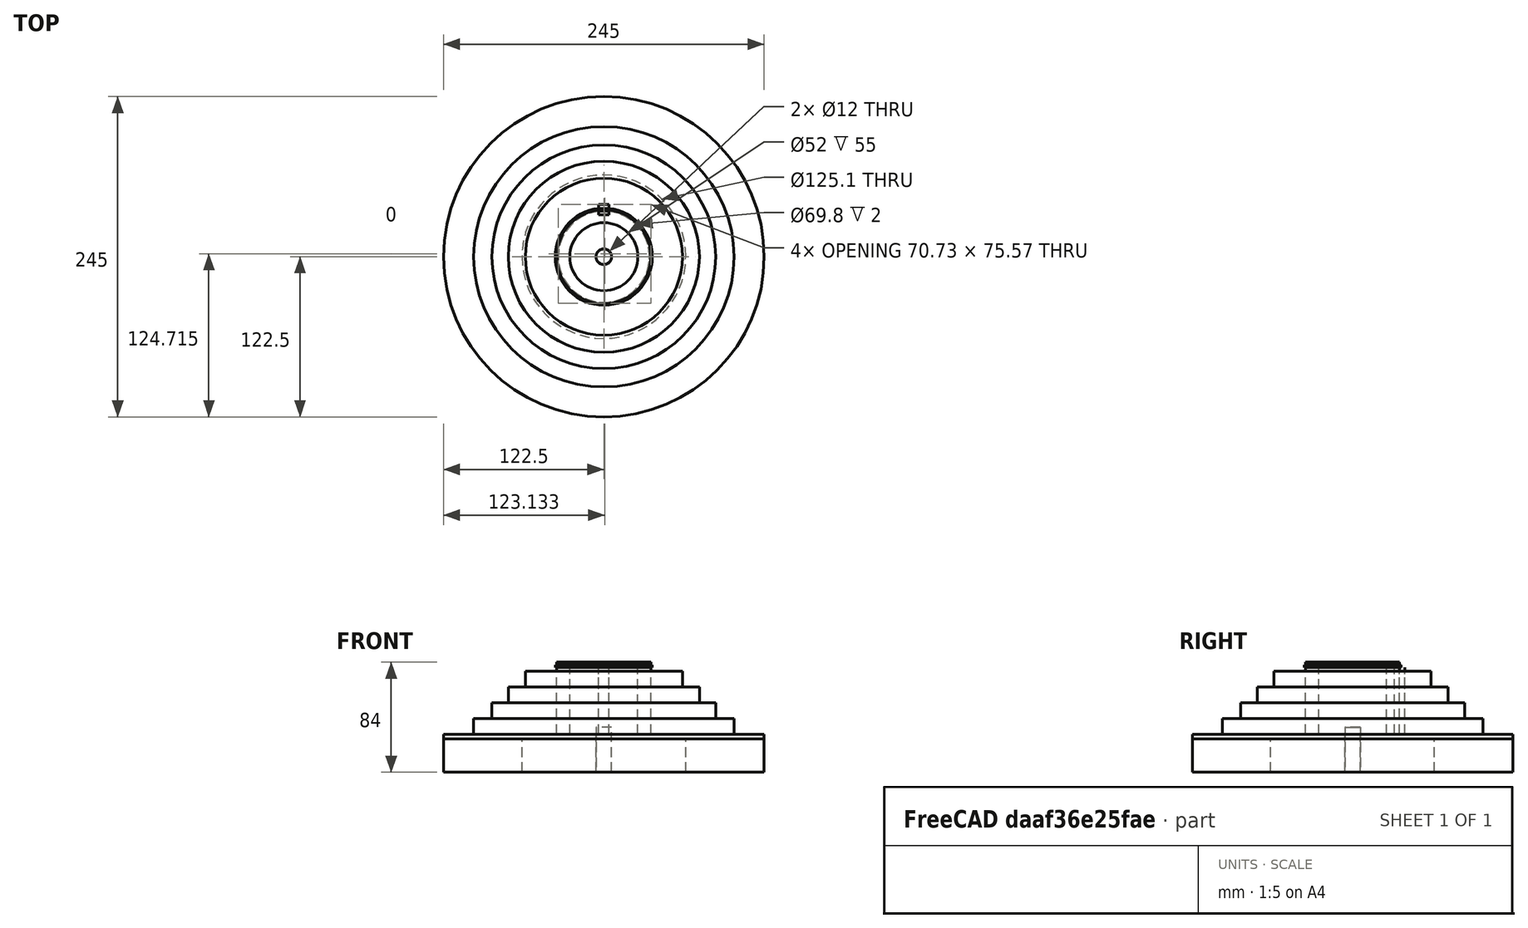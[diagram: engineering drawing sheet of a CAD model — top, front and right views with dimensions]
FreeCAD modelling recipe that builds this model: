
FCSTD DOCUMENT  (FreeCAD 1.0R39319 (Git))
Label: inertia_cylinder-custom
License: All rights reserved
LicenseURL: https://en.wikipedia.org/wiki/All_rights_reserved
objects: TechDraw::DrawViewDimension×42, Part::FeaturePython×10, TechDraw::DrawProjGroupItem×9, Part::Cut×5, TechDraw::DrawSVGTemplate×5, TechDraw::DrawViewAnnotation×5, TechDraw::DrawViewImage×5, TechDraw::DrawPage×5, Spreadsheet::Sheet×4, Part::Compound×3, Part::Box×2, App::DocumentObjectGroup×2, TechDraw::DrawViewSection×2, Part::Cylinder×1, PartDesign::FeatureBase×1, PartDesign::Body×1, Part::MultiFuse×1
note: 89 computed .brp shape members not serialized (recipe doc carries the construction recipe); baked Part::Feature solids carry a one-line shape summary decoded from their .brp

FEATURE [Spreadsheet::Sheet] Spreadsheet  label="fixedParameters"
  cells = A1='spacial properties; I1(color_scale)='color scale; A2='tubes; B2='radiusInner; C2='radiusOuter; D2='length; J2='Have to confirm; A3='contactDrum; B3(contactDrum_radiusInner)==threadedRod_radius; C3(contactDrum_radiusOuter)==25.14 mm; D3(contactDrum_length)==80.84 mm; J3='taken from spreadsheet; A4='disk; B4(disk_radiusInner)==threadedRod_radius; C4(disk_radiusOuter)==62.55 mm; D4(disk_length)==25.23 mm; J4='irrelevant but have to confirm; C5=125.11; J5='irrelevant; A6='cylinders; B6='radius; C6='length; A7='threadedRod; B7(threadedRod_radius)==6 mm; C7(threadedShaft_extrusionLength)==8.97 mm; A8='wheel; B8(wheel_radius)==0.3406 m; C8(wheel_length)==47 mm; A10='clearanceSpace; B10='horizontal; C10='vertical; D10='vertical mid; A11='diskFrame; B11(diskFrame_h_clearance)==68 mm; C11(diskFrame_v_clearance)==120 mm; D11==39 mm; A13='matter properties; A14='mass; B14='bike; A15='mass; B15(bike_mass)==15 kg; A17='materials; B17='density; A18='stainlessSteel; B18(ss_density)==7.85 g / ml; A19='dMetal; B19(dMetal_density)==ss_density; A20='all; B20='density; C20='mass; A21='wheel; B21='non-uniform-mix; C21(wheel_mass)==2 kg; A22='contactDrum; B22(contactDrum_density)==dMetal_density; A23='disk; B23(disk_density)==dMetal_density; A24='threadedRod; B24(threadedRod_density)==dMetal_density; A25='flywheel; B25(flywheel_density)==ss_density; A26='hub; B26(hub_density)==ss_density; A27='extendingDrum; B27(extendingDrum_density)==ss_density; A28='weightPlate; B28(weightPlate_density)==ss_density; A29='wp_ed_key; B29(wp_ed_key_density)==ss_density; A30='keyHandle; B30(keyHandle_density)==ss_density; A31='plateSecurer_screw; B31(plateSecurer_screw_density)==ss_density; A32='plateSecurerPlate; B32(plateSecurer_plateDensity)==ss_density; A33='constants; B33='Value; A34='pi; B34(pi_value)=3.1415
FEATURE [Spreadsheet::Sheet] Spreadsheet001  label="calculatedParameters"
  cells = A1='tubes; B1='radiusInner; C1='radiusOuter; D1='length; E1='density; F1='mass; G1='area out; H1='area in; I1='area; J1='Volume; A2='contactDrum; B2(contactDrum_radiusInner)==<<fixedParameters>>.contactDrum_radiusInner; C2(contactDrum_radiusOuter)==<<fixedParameters>>.contactDrum_radiusOuter; D2(contactDrum_length)==<<fixedParameters>>.contactDrum_length; E2(contactDrum_density)==<<fixedParameters>>.contactDrum_density; F2(contactDrum_mass)==<<fixedParameters>>.contactDrum_density * contactDrum_volume; G2(contactDrum_areaOut)==contactDrum_radiusOuter * contactDrum_radiusOuter * <<fixedParameters>>.pi_value; H2(contactDrum_areaIn)==contactDrum_radiusInner * contactDrum_radiusInner * <<fixedParameters>>.pi_value; I2(contactDrum_area)==contactDrum_areaOut - contactDrum_areaIn; J2(contactDrum_volume)==contactDrum_area * contactDrum_length; A3='disk; B3(disk_radiusInner)==<<fixedParameters>>.disk_radiusInner; C3(disk_radiusOuter)==<<fixedParameters>>.disk_radiusOuter; D3(disk_length)==<<fixedParameters>>.disk_length; E3(disk_density)==<<fixedParameters>>.disk_density; F3(disk_mass)==<<fixedParameters>>.disk_density * disk_volume; G3(disk_areaOut)==disk_radiusOuter * disk_radiusOuter * <<fixedParameters>>.pi_value; H3(disk_areaIn)==disk_radiusInner * disk_radiusInner * <<fixedParameters>>.pi_value; I3(disk_area)==disk_areaOut - disk_areaIn; J3(disk_volume)==disk_area * disk_length; A4='flywheel; B4(flywheel_radiusInner)==disk_radiusOuter; C4(flywheel_radiusOuter)==flywheel_radiusInner + <<properties>>.flywheel_radThickness; D4(flywheel_length)==<<fixedParameters>>.disk_length; E4(flywheel_density)==<<fixedParameters>>.flywheel_density; F4(flywheel_mass)==<<fixedParameters>>.flywheel_density * flywheel_volume; G4(flywheel_areaOut)==flywheel_radiusOuter * flywheel_radiusOuter * <<fixedParameters>>.pi_value; H4(flywheel_areaIn)==flywheel_radiusInner * flywheel_radiusInner * <<fixedParameters>>.pi_value; I4(flywheel_area)==flywheel_areaOut - flywheel_areaIn; J4(flywheel_volume)==flywheel_area * flywheel_length; A5='hub; B5(hub_radiusInner)==<<fixedParameters>>.threadedRod_radius; C5(hub_radiusOuter)==flywheel_radiusOuter; D5(hub_length)==<<properties>>.hub_thickness; E5(hub_density)==<<fixedParameters>>.hub_density; F5(hub_mass)==hub_volume * <<fixedParameters>>.hub_density; G5(hub_areaOut)==hub_radiusOuter * hub_radiusOuter * <<fixedParameters>>.pi_value; H5(hub_areaIn)==hub_radiusInner * hub_radiusInner * <<fixedParameters>>.pi_value; I5(hub_area)==hub_areaOut - hub_areaIn; J5(hub_volume)==hub_area * hub_length; A6='extendingDrum; B6(extendingDrum_radiusInner)==<<properties>>.nut_clearance; C6(extendingDrum_radiusOuter)==extendingDrum_radiusInner + <<properties>>.extendingDrum_radiusThickness; D6(extendingDrum_length)==<<fixedParameters>>.diskFrame_h_clearance - <<properties>>.weightPlate_thickness - <<properties>>.weightPlate_insertionTolerance; E6(extendingDrum_density)==<<fixedParameters>>.extendingDrum_density; F6(extendingDrum_mass)==<<fixedParameters>>.extendingDrum_density * extendingDrum_volume; G6(extendingDrum_areaOut)==extendingDrum_radiusOuter * extendingDrum_radiusOuter * <<fixedParameters>>.pi_value; H6(extendingDrum_areaIn)==extendingDrum_radiusInner * extendingDrum_radiusInner * <<fixedParameters>>.pi_value; I6(extendingDrum_area)==extendingDrum_areaOut - extendingDrum_areaIn; J6(extendingDrum_volume)==extendingDrum_area * extendingDrum_length; A7='w1; B7(weightPlate_radiusInner)==extendingDrum_radiusOuter; C7(w1_radiusOuter)==99.5 mm; D7(weightPlate_thickness)==<<properties>>.weightPlate_thickness; E7(weightPlate_density)==<<fixedParameters>>.weightPlate_density; F7(w1_mass)==w1_volume * weightPlate_density; G7(w1_areaOut)==w1_radiusOuter * w1_radiusOuter * <<fixedParameters>>.pi_value; H7(w_areaIn)==weightPlate_radiusInner * weightPlate_radiusInner * <<fixedParameters>>.pi_value; I7(w1_area)==w1_areaOut - w_areaIn; J7(w1_volume)==w1_area * weightPlate_thickness; A8='w2; C8(w2_radiusOuter)==85.5 mm; F8(w2_mass)==w2_volume * weightPlate_density; G8(w2_areaOut)==w2_radiusOuter * w2_radiusOuter * <<fixedParameters>>.pi_value; I8(w2_area)==w2_areaOut - w_areaIn; J8(w2_volume)==w2_area * weightPlate_thickness; A9='w3; C9(w3_radiusOuter)==73 mm; F9(w3_mass)==w3_volume * weightPlate_density; G9(w3_areaOut)==w3_radiusOuter * w3_radiusOuter * <<fixedParameters>>.pi_value; I9(w3_area)==w3_areaOut - w_areaIn; J9(w3_volume)==w3_area * weightPlate_thickness; A10='w4; C10(w4_radiusOuter)==60 mm; F10(w4_mass)==w4_volume * weightPlate_density; G10(w4_areaOut)==w4_radiusOuter * w4_radiusOuter * <<fixedParameters>>.pi_value; I10(w4_area)==w4_areaOut - w_areaIn; J10(w4_volume)==w4_area * weightPlate_thickness; A12='cuboids; B12='height; C12='width; D12='length; F12='mass; G12='area; A13='weightPlate_extendingDisk_key; B13(wp_ed_key_height)==<<properties>>.wP_eD_penetrationHeight; C13(wp_ed_key_width)==<<properties>>.wP_eD_key_penetrationWidth; D13(wp_ed_key_length)==extendingDrum_length; E13(wp_ed_key_density)==<<fixedParameters>>.wp_ed_key_density; F13(wp_ed_key_mass)==wp_ed_key_volume * wp_ed_key_density; G13(wp_ed_key_area)==wp_ed_key_height * wp_ed_key_width; J13(wp_ed_key_volume)==wp_ed_key_area * wp_ed_key_length; A14='cylinders; B14='radius; D14='length; E14='density; F14='mass; G14='area; J14='volume; A15='threadedShaft; B15(threadedShaft_radius)==<<fixedParameters>>.threadedRod_radius; D15(threadedShaft_length)==<<fixedParameters>>.threadedShaft_extrusionLength + disk_length; E15(threadedShaft_density)==<<fixedParameters>>.threadedRod_density; F15(threadedShaft_mass)==threadedShaft_volume * threadedShaft_density; G15(threadedShaft_area)==threadedShaft_radius * threadedShaft_radius * <<fixedParameters>>.pi_value; J15(threadedShaft_volume)==threadedShaft_area * threadedShaft_length; A16='wheel; B16(wheel_radius)==<<fixedParameters>>.wheel_radius; D16(wheel_length)==<<fixedParameters>>.wheel_length; E16(wheel_density)==wheel_mass / wheel_volume; F16(wheel_mass)==<<fixedParameters>>.wheel_mass; G16(wheel_area)==wheel_radius * wheel_radius * <<fixedParameters>>.pi_value; J16(wheel_volume)==wheel_length * wheel_area; A18='TOTAL for setup; F18==sum(F4:F10; F13); J18==sum(J4:J10; J13); A20='negative; A21='negative tubes; A22='circlip_grove; B22(circlip_grove_radiusInner)==circlip_grove_radiusOuter - <<properties>>.circlip_grove_depth; C22(circlip_grove_radiusOuter)==extendingDrum_radiusOuter; D22(circlip_grove_length)==<<properties>>.circlip_grove_width
FEATURE [Spreadsheet::Sheet] Spreadsheet002  label="properties"
  cells = A1='spacial properties; A2='tubes; B2='radius 'thickness; D2='key; E2='penetrationHeight; F2='penetrationWidth; A3='flywheel; B3(flywheel_radThickness)==59.95 mm; D3='weightPlate_extendingDrum_key; E3(wP_eD_penetrationHeight)==8 mm; F3(wP_eD_key_penetrationWidth)==8 mm; A4='extendingDrum; B4(extendingDrum_radiusThickness)==10 mm; D4='key; E4='extraLength; A5='tubes; B5='extending thickness; D5='key; E5(key_extraLength)==0 mm; A6='hub; B6(hub_thickness)==3.77 mm; A7='weightPlate; B7(weightPlate_thickness)==1.2 cm; D7='plateSecurer; E7='screwLength; F7='plateSecuringRadius; G7='plateThickness; D8='plateSecurer; E8(plateSecurer_screwLength)==1 cm; F8(plateSecuring_plate_radius)==5 cm; G8(plateSecurer_plateHeight)==2 mm; A9='tolerance; B9='insertionTolerance; A10='weightPlate; B10(weightPlate_insertionTolerance)==1 mm; D10='grove circlip; E10='width; F10='depth; G10='gap; A11='tolerance; B11='fittingTolerance; D11='circlip; E11(circlip_grove_width)==2 mm; F11(circlip_grove_depth)==1.1 mm; G11(circlip_grove_gap)==2 mm; A12='fitting tolerance; B12(fittingTolerance)==0.08 mm; D13='nut; E13='clearance for nut; A14='matter properties; D14='tool; E14(nut_clearance)==25.79 mm + 0.21 mm; A15='target mass; B15='mass; A16='rider; B16(rider_mass)==70 kg
FEATURE [Part::FeaturePython] Tube  label="flywheel"  # WARN: FeaturePython — macro-defined, semantics opaque (R4)
  AttacherType = Attacher::AttachEngine3D
  Height = 25.23
  InnerRadius = 62.55
  OuterRadius = 122.5
  expr: Height = <<calculatedParameters>>.flywheel_length
  expr: InnerRadius = <<calculatedParameters>>.flywheel_radiusInner
  expr: OuterRadius = <<calculatedParameters>>.flywheel_radiusOuter
FEATURE [Part::FeaturePython] Tube001  label="disk"  # WARN: FeaturePython — macro-defined, semantics opaque (R4)
  AttacherType = Attacher::AttachEngine3D
  Height = 25.23
  InnerRadius = 6
  OuterRadius = 62.55
  expr: Height = <<fixedParameters>>.disk_length
  expr: InnerRadius = <<fixedParameters>>.disk_radiusInner
  expr: OuterRadius = <<fixedParameters>>.disk_radiusOuter
FEATURE [Part::FeaturePython] Tube002  label="hub"  # WARN: FeaturePython — macro-defined, semantics opaque (R4)
  AttacherType = Attacher::AttachEngine3D
  Height = 3.77
  InnerRadius = 6
  OuterRadius = 122.5
  Placement = pos=(0,0,25.23) rot=(0,0,1;0rad)
  expr: .Placement.Base.z = <<flywheel>>.Placement.Base.z + <<calculatedParameters>>.flywheel_length
  expr: Height = <<calculatedParameters>>.hub_length
  expr: InnerRadius = <<calculatedParameters>>.hub_radiusInner
  expr: OuterRadius = <<calculatedParameters>>.hub_radiusOuter
FEATURE [Part::FeaturePython] Tube003  label="extendingDrum"  # WARN: FeaturePython — macro-defined, semantics opaque (R4)
  AttacherType = Attacher::AttachEngine3D
  Height = 55
  InnerRadius = 26
  OuterRadius = 36
  Placement = pos=(0,0,29) rot=(0,0,1;0rad)
  expr: .Placement.Base.z = <<hub>>.Placement.Base.z + <<calculatedParameters>>.hub_length
  expr: Height = <<calculatedParameters>>.extendingDrum_length
  expr: InnerRadius = <<calculatedParameters>>.extendingDrum_radiusInner
  expr: OuterRadius = <<calculatedParameters>>.extendingDrum_radiusOuter
FEATURE [Part::Box] Box  label="wp_ed_key"
  AttacherType = Attacher::AttachEngine3D
  Height = 55
  Length = 8
  Placement = pos=(-4,32,29) rot=(0,0,1;0rad)
  Width = 8
  expr: .Placement.Base.x = -<<calculatedParameters>>.wp_ed_key_width / 2
  expr: .Placement.Base.y = <<extendingDrum>>.OuterRadius - <<calculatedParameters>>.wp_ed_key_height / 2
  expr: .Placement.Base.z = <<hub>>.Placement.Base.z + <<calculatedParameters>>.hub_length
  expr: Height = <<calculatedParameters>>.wp_ed_key_length
  expr: Length = <<calculatedParameters>>.wp_ed_key_width
  expr: Width = <<calculatedParameters>>.wp_ed_key_height
FEATURE [Spreadsheet::Sheet] Spreadsheet003  label="inertia"
  cells = A1='addonSetup; C1='moment of inertia; D1='inertia; E1='ideal moi; F1='error; H1='moi per effective kg; I1='plate weights required; A2='tubes; B2='contactDrum; C2(moi_contactDrum)==<<calculatedParameters>>.contactDrum_radiusOuter * <<calculatedParameters>>.contactDrum_radiusOuter * <<calculatedParameters>>.contactDrum_mass * 0.5 - <<calculatedParameters>>.contactDrum_radiusInner * <<calculatedParameters>>.contactDrum_radiusInner * <<calculatedParameters>>.contactDrum_mass * 0.5; D2==0 kg; H2(moi_pkg)==625 (mm ^ 2); I2(w1_t_kg)==20 kg; B3='disk; C3(moi_disk)==<<calculatedParameters>>.disk_radiusOuter * <<calculatedParameters>>.disk_radiusOuter * <<calculatedParameters>>.disk_mass * 0.5 - <<calculatedParameters>>.disk_radiusInner * <<calculatedParameters>>.disk_radiusInner * <<calculatedParameters>>.disk_mass * 0.5; I3(w2_t_kg)==10 kg; B4='flywheel; C4(moi_flywheel)==<<calculatedParameters>>.flywheel_radiusOuter * <<calculatedParameters>>.flywheel_radiusOuter * <<calculatedParameters>>.flywheel_mass * 0.5 - <<calculatedParameters>>.flywheel_radiusInner * <<calculatedParameters>>.flywheel_radiusInner * <<calculatedParameters>>.flywheel_mass * 0.5; I4(w3_t_kg)==5 kg; B5='hub; C5(moi_hub)==<<calculatedParameters>>.hub_radiusOuter * <<calculatedParameters>>.hub_radiusOuter * <<calculatedParameters>>.hub_mass * 0.5 - <<calculatedParameters>>.hub_radiusInner * <<calculatedParameters>>.hub_radiusInner * <<calculatedParameters>>.hub_mass * 0.5; I5(w4_t_kg)==2 kg; B6='extendingDrum; C6(moi_extendingDrum)==<<calculatedParameters>>.extendingDrum_radiusOuter * <<calculatedParameters>>.extendingDrum_radiusOuter * <<calculatedParameters>>.extendingDrum_mass * 0.5 - <<calculatedParameters>>.contactDrum_radiusInner * <<calculatedParameters>>.extendingDrum_radiusInner * <<calculatedParameters>>.extendingDrum_mass * 0.5; A7='cylinders; B7='threadedShaft; C7(moi_threadedShaft)==<<calculatedParameters>>.threadedShaft_radius * <<calculatedParameters>>.threadedShaft_radius * <<calculatedParameters>>.threadedShaft_mass * 0.5; A8='total; C8(moi_setup_total)==sum(C2:C7); D8(inertia_setup_total)==sum(D2:D7); E8(moi_ideal_setup_total)==moi_pkg * 53; A9='weightPlates; B10='weightPlate1; C10(w1_moi)==<<calculatedParameters>>.w1_radiusOuter * <<calculatedParameters>>.w1_radiusOuter * <<calculatedParameters>>.w1_mass * 0.5 - <<calculatedParameters>>.weightPlate_radiusInner * <<calculatedParameters>>.weightPlate_radiusInner * <<calculatedParameters>>.w1_mass * 0.5; D10==0 g; E10(ideal_moi_w1)==moi_pkg * w1_t_kg; F10==ideal_moi_w1 - w1_moi; G10==F10 / H2; B11='weightPlate2; C11(w2_moi)==<<calculatedParameters>>.w2_radiusOuter * <<calculatedParameters>>.w2_radiusOuter * <<calculatedParameters>>.w2_mass * 0.5 - <<calculatedParameters>>.weightPlate_radiusInner * <<calculatedParameters>>.weightPlate_radiusInner * <<calculatedParameters>>.w2_mass * 0.5; E11(ideal_moi_w2)==moi_pkg * w2_t_kg; F11==ideal_moi_w2 - w2_moi; G11==F11 / H2; B12='weightPlate3; C12(w3_moi)==<<calculatedParameters>>.w3_radiusOuter * <<calculatedParameters>>.w3_radiusOuter * <<calculatedParameters>>.w3_mass * 0.5 - <<calculatedParameters>>.weightPlate_radiusInner * <<calculatedParameters>>.weightPlate_radiusInner * <<calculatedParameters>>.w3_mass * 0.5; E12(ideal_moi_w3)==moi_pkg * w3_t_kg; F12==ideal_moi_w3 - w3_moi; G12==F12 / H2; B13='weightPlate4; C13(w4_moi)==<<calculatedParameters>>.w4_radiusOuter * <<calculatedParameters>>.w4_radiusOuter * <<calculatedParameters>>.w4_mass * 0.5 - <<calculatedParameters>>.weightPlate_radiusInner * <<calculatedParameters>>.weightPlate_radiusInner * <<calculatedParameters>>.w4_mass * 0.5; E13(ideal_moi_w4)==moi_pkg * w4_t_kg; F13==ideal_moi_w4 - w4_moi; G13==F13 / H2; B14='total; C14(moi_weightPlates_total)==sum(C10:C13); E14(moi_ideal)==sum(E10:E13); F14==moi_ideal - moi_weightPlates_total; G14==F14 / H2; A15='completeStetup; C15(completeSetup_moi)==moi_setup_total + moi_weightPlates_total; D15==sum(D10:D14); E15(ideal_total_moi)==moi_setup_total + moi_ideal; F15==ideal_total_moi - completeSetup_moi; G15==F15 / H2; A17='target; B18='bike; C18(bike_moi)==0 kg * 0 m * 0 m; D18(bike_inertia)==<<fixedParameters>>.bike_mass; B19='rider; C19(rider_moi)==0 m * 0 m * 0 kg; D19(rider_inertiia)==<<properties>>.rider_mass; A20='total; C20(moi_target_total)==bike_moi + rider_moi; D20==bike_inertia + rider_inertiia
FEATURE [App::DocumentObjectGroup] Group  label="dimentionCalculations"
  Group = -> [Spreadsheet002,Spreadsheet001,Spreadsheet,Spreadsheet003]
FEATURE [Part::FeaturePython] Tube004  label="w1"  # WARN: FeaturePython — macro-defined, semantics opaque (R4)
  AttacherType = Attacher::AttachEngine3D
  Height = 12
  InnerRadius = 36
  OuterRadius = 99.5
  Placement = pos=(0,0,29) rot=(0,0,1;0rad)
  expr: .Placement.Base.z = <<hub>>.Placement.Base.z + <<hub>>.Height
  expr: Height = <<calculatedParameters>>.weightPlate_thickness
  expr: InnerRadius = <<calculatedParameters>>.weightPlate_radiusInner
  expr: OuterRadius = <<calculatedParameters>>.w1_radiusOuter
FEATURE [Part::FeaturePython] Tube005  label="w2"  # WARN: FeaturePython — macro-defined, semantics opaque (R4)
  AttacherType = Attacher::AttachEngine3D
  Height = 12
  InnerRadius = 36
  OuterRadius = 85.5
  Placement = pos=(0,0,41) rot=(0,0,1;0rad)
  expr: .Placement.Base.z = <<hub>>.Placement.Base.z + <<hub>>.Height + <<calculatedParameters>>.weightPlate_thickness
  expr: Height = <<calculatedParameters>>.weightPlate_thickness
  expr: InnerRadius = <<calculatedParameters>>.weightPlate_radiusInner
  expr: OuterRadius = <<calculatedParameters>>.w2_radiusOuter
FEATURE [Part::FeaturePython] Tube006  label="w3"  # WARN: FeaturePython — macro-defined, semantics opaque (R4)
  AttacherType = Attacher::AttachEngine3D
  Height = 12
  InnerRadius = 36
  OuterRadius = 73
  Placement = pos=(0,0,53) rot=(0,0,1;0rad)
  expr: .Placement.Base.z = <<hub>>.Placement.Base.z + <<hub>>.Height + 2 * <<calculatedParameters>>.weightPlate_thickness
  expr: Height = <<calculatedParameters>>.weightPlate_thickness
  expr: InnerRadius = <<calculatedParameters>>.weightPlate_radiusInner
  expr: OuterRadius = <<calculatedParameters>>.w3_radiusOuter
FEATURE [Part::Cut] Cut001  label="w1_keyed"
  Base = -> Tube004
  Refine = true
  Tool = -> Box
FEATURE [Part::Cut] Cut002  label="w2_keyed"
  Base = -> Tube005
  Refine = true
  Tool = -> Box
FEATURE [Part::Cut] Cut003  label="w3_keyed"
  Base = -> Tube006
  Refine = true
  Tool = -> Box
FEATURE [Part::Box] Box001  label="key"
  AttacherType = Attacher::AttachEngine3D
  Height = 51
  Length = 8
  Placement = pos=(-4,32,29) rot=(0,0,1;0rad)
  Width = 8
  expr: .Placement.Base.x = <<wp_ed_key>>.Placement.Base.x
  expr: .Placement.Base.y = <<wp_ed_key>>.Placement.Base.y
  expr: .Placement.Base.z = <<wp_ed_key>>.Placement.Base.z
  expr: Height = <<wp_ed_key>>.Height - <<properties>>.circlip_grove_gap - <<properties>>.circlip_grove_width
  expr: Length = <<wp_ed_key>>.Length
  expr: Width = <<wp_ed_key>>.Width
FEATURE [Part::Cylinder] Cylinder  label="threadedShaft"
  Angle = 360
  AttacherType = Attacher::AttachEngine3D
  FirstAngle = 0
  Height = 34.2
  Radius = 5.92
  SecondAngle = 0
  expr: .Placement.Base.z = 0
  expr: Height = <<calculatedParameters>>.threadedShaft_length
  expr: Radius = <<calculatedParameters>>.threadedShaft_radius - <<properties>>.fittingTolerance
FEATURE [Part::Compound] Compound002  label="disk_with_shaft"
  Links = -> [Cylinder,Tube001]
FEATURE [TechDraw::DrawSVGTemplate] Template003
  Height = 210
  Orientation = 1
  Template = /app/share/Mod/TechDraw/Templates/Default_Template_A4_Landscape.svg
  Width = 297
FEATURE [Part::FeaturePython] Tube008  label="circlip_grove"  # WARN: FeaturePython — macro-defined, semantics opaque (R4)
  AttacherType = Attacher::AttachEngine3D
  Height = 2
  InnerRadius = 34.9
  OuterRadius = 36
  Placement = pos=(0,0,80) rot=(0,0,-1;0.05236rad)
  expr: .Placement.Base.z = <<extendingDrum>>.Placement.Base.z + <<extendingDrum>>.Height - <<calculatedParameters>>.circlip_grove_length - <<properties>>.circlip_grove_gap
  expr: Height = <<calculatedParameters>>.circlip_grove_length
  expr: InnerRadius = <<calculatedParameters>>.circlip_grove_radiusInner
  expr: OuterRadius = <<calculatedParameters>>.circlip_grove_radiusOuter
FEATURE [PartDesign::FeatureBase] Clone
  BaseFeature = -> Box
  Placement = pos=(-4,32,29) rot=(0,0,1;0rad)
  Suppressed = false
  expr: .Placement.Base.x = <<wp_ed_key>>.Placement.Base.x
  expr: .Placement.Base.y = <<wp_ed_key>>.Placement.Base.y
  expr: .Placement.Base.z = <<wp_ed_key>>.Placement.Base.z
FEATURE [PartDesign::Body] Body  label="keyClone1"
  AllowCompound = false
  Group = -> [Clone]
  Origin = -> Origin
  Tip = -> Clone
FEATURE [Part::MultiFuse] Fusion  label="grove_and_key"
  Refine = true
  Shapes = -> [Body,Tube008]
FEATURE [Part::Cut] Cut  label="extendingDisk_grovedNdKeyed"
  Base = -> Tube003
  Refine = true
  Tool = -> Fusion
FEATURE [Part::Compound] Compound  label="additive_assembly"
  Links = -> [Cut,Tube002,Tube]
FEATURE [TechDraw::DrawSVGTemplate] Template004
  Height = 210
  Orientation = 1
  Template = /app/share/Mod/TechDraw/Templates/Default_Template_A4_Landscape.svg
  Width = 297
FEATURE [Part::FeaturePython] Tube009  label="w4"  # WARN: FeaturePython — macro-defined, semantics opaque (R4)
  AttacherType = Attacher::AttachEngine3D
  Height = 12
  InnerRadius = 36
  OuterRadius = 60
  Placement = pos=(0,0,65) rot=(0,0,1;0rad)
  expr: .Placement.Base.z = <<hub>>.Placement.Base.z + <<hub>>.Height + 3 * <<calculatedParameters>>.weightPlate_thickness
  expr: Height = <<calculatedParameters>>.weightPlate_thickness
  expr: InnerRadius = <<calculatedParameters>>.weightPlate_radiusInner
  expr: OuterRadius = <<calculatedParameters>>.w4_radiusOuter
FEATURE [Part::Cut] Cut004  label="w4_keyed"
  Base = -> Tube009
  Refine = true
  Tool = -> Box
FEATURE [Part::Compound] Compound001  label="weights_keyed"
  Links = -> [Cut003,Cut002,Cut001,Cut004]
FEATURE [TechDraw::DrawProjGroupItem] View019
  CoarseView = false
  Direction = (0,-1,0)
  Focus = 100
  HardHidden = false
  IsoCount = 0
  IsoHidden = false
  IsoVisible = false
  LockPosition = false
  Perspective = false
  Rotation = 0
  RotationVector = (1,0,0)
  ScaleType = 0
  ScrubCount = 1
  SeamHidden = false
  SeamVisible = false
  SmoothHidden = false
  SmoothVisible = true
  Source = -> [Compound001]
  Type = 0
  X = 124.333
  XDirection = (1,0,0)
  Y = 114.233
FEATURE [Part::FeaturePython] Tube010  label="circlip"  # WARN: FeaturePython — macro-defined, semantics opaque (R4)
  AttacherType = Attacher::AttachEngine3D
  Height = 2
  InnerRadius = 34.9
  OuterRadius = 37.1
  Placement = pos=(0,0,80) rot=(0,0,1;0rad)
  expr: .Placement.Base.z = <<extendingDrum>>.Placement.Base.z + <<extendingDrum>>.Height - <<properties>>.circlip_grove_gap - <<properties>>.circlip_grove_width / 2 - Height / 2
  expr: Height = <<properties>>.circlip_grove_width
  expr: InnerRadius = <<extendingDrum>>.OuterRadius - <<properties>>.circlip_grove_depth
  expr: OuterRadius = <<calculatedParameters>>.extendingDrum_radiusOuter + <<properties>>.circlip_grove_depth
FEATURE [TechDraw::DrawViewDimension] Dimension079
  AngleOverride = false
  Arbitrary = false
  ArbitraryTolerances = false
  BoxCorners = (2) [(-99.3,-24,-1e-07),(99.3,24,1e-07)]
  EqualTolerance = true
  ExtensionAngle = 0
  FormatSpec = %.2w
  FormatSpecOverTolerance = %+.2w
  FormatSpecUnderTolerance = %+.2w
  Inverted = false
  LineAngle = 0
  LockPosition = false
  MeasureType = 1
  OverTolerance = 0
  References2D = -> [View019]
  Rotation = 0
  ScaleType = 0
  TheoreticalExact = false
  Type = 2
  UnderTolerance = 0
  X = -112.919
  Y = -18
FEATURE [TechDraw::DrawViewDimension] Dimension080
  AngleOverride = false
  Arbitrary = false
  ArbitraryTolerances = false
  BoxCorners = (2) [(-99.3,-24,-1e-07),(99.3,24,1e-07)]
  EqualTolerance = true
  ExtensionAngle = 0
  FormatSpec = %.2w
  FormatSpecOverTolerance = %+.2w
  FormatSpecUnderTolerance = %+.2w
  Inverted = false
  LineAngle = 0
  LockPosition = false
  MeasureType = 1
  OverTolerance = 0
  References2D = -> [View019]
  Rotation = 0
  ScaleType = 0
  TheoreticalExact = false
  Type = 2
  UnderTolerance = 0
  X = -112.919
  Y = -6
FEATURE [TechDraw::DrawViewDimension] Dimension081
  AngleOverride = false
  Arbitrary = false
  ArbitraryTolerances = false
  BoxCorners = (2) [(-99.3,-24,-1e-07),(99.3,24,1e-07)]
  EqualTolerance = true
  ExtensionAngle = 0
  FormatSpec = %.2w
  FormatSpecOverTolerance = %+.2w
  FormatSpecUnderTolerance = %+.2w
  Inverted = false
  LineAngle = 0
  LockPosition = false
  MeasureType = 1
  OverTolerance = 0
  References2D = -> [View019]
  Rotation = 0
  ScaleType = 0
  TheoreticalExact = false
  Type = 2
  UnderTolerance = 0
  X = -112.919
  Y = 6
FEATURE [TechDraw::DrawViewDimension] Dimension082
  AngleOverride = false
  Arbitrary = false
  ArbitraryTolerances = false
  BoxCorners = (2) [(-99.3,-24,-1e-07),(99.3,24,1e-07)]
  EqualTolerance = true
  ExtensionAngle = 0
  FormatSpec = %.2w
  FormatSpecOverTolerance = %+.2w
  FormatSpecUnderTolerance = %+.2w
  Inverted = false
  LineAngle = 0
  LockPosition = false
  MeasureType = 1
  OverTolerance = 0
  References2D = -> [View019]
  Rotation = 0
  ScaleType = 0
  TheoreticalExact = false
  Type = 2
  UnderTolerance = 0
  X = -112.919
  Y = 18
FEATURE [TechDraw::DrawViewDimension] Dimension083
  AngleOverride = false
  Arbitrary = false
  ArbitraryTolerances = false
  BoxCorners = (2) [(-99.3,-24,-1e-07),(99.3,24,1e-07)]
  EqualTolerance = true
  ExtensionAngle = 0
  FormatSpec = %.2w
  FormatSpecOverTolerance = %+.2w
  FormatSpecUnderTolerance = %+.2w
  Inverted = false
  LineAngle = 0
  LockPosition = false
  MeasureType = 1
  OverTolerance = 0
  References2D = -> [View019]
  Rotation = 0
  ScaleType = 0
  TheoreticalExact = false
  Type = 1
  UnderTolerance = 0
  X = 0
  Y = 44.9715
FEATURE [TechDraw::DrawViewDimension] Dimension084
  AngleOverride = false
  Arbitrary = false
  ArbitraryTolerances = false
  BoxCorners = (2) [(-99.3,-24,-1e-07),(99.3,24,1e-07)]
  EqualTolerance = true
  ExtensionAngle = 0
  FormatSpec = %.2w
  FormatSpecOverTolerance = %+.2w
  FormatSpecUnderTolerance = %+.2w
  Inverted = false
  LineAngle = 0
  LockPosition = false
  MeasureType = 1
  OverTolerance = 0
  References2D = -> [View019]
  Rotation = 0
  ScaleType = 0
  TheoreticalExact = false
  Type = 1
  UnderTolerance = 0
  X = 0
  Y = 58.3067
FEATURE [TechDraw::DrawViewDimension] Dimension085
  AngleOverride = false
  Arbitrary = false
  ArbitraryTolerances = false
  BoxCorners = (2) [(-99.3,-24,-1e-07),(99.3,24,1e-07)]
  EqualTolerance = true
  ExtensionAngle = 0
  FormatSpec = %.2w
  FormatSpecOverTolerance = %+.2w
  FormatSpecUnderTolerance = %+.2w
  Inverted = false
  LineAngle = 0
  LockPosition = false
  MeasureType = 1
  OverTolerance = 0
  References2D = -> [View019]
  Rotation = 0
  ScaleType = 0
  TheoreticalExact = false
  Type = 1
  UnderTolerance = 0
  X = 0
  Y = 72.9493
FEATURE [TechDraw::DrawProjGroupItem] View021  label="View022"
  CoarseView = false
  Direction = (0,0,1)
  Focus = 100
  HardHidden = false
  IsoCount = 0
  IsoHidden = false
  IsoVisible = false
  LockPosition = false
  Perspective = false
  Rotation = 0
  RotationVector = (1,0,0)
  Scale = 0.5
  ScaleType = 2
  ScrubCount = 1
  SeamHidden = false
  SeamVisible = false
  SmoothHidden = false
  SmoothVisible = true
  Source = -> [Cut003]
  Type = 0
  X = 53.611
  XDirection = (1,0,0)
  Y = 46.8909
FEATURE [TechDraw::DrawViewDimension] Dimension087
  AngleOverride = false
  Arbitrary = false
  ArbitraryTolerances = false
  BoxCorners = (2) [(-36.3,-36.3,0),(36.3,36.3,0)]
  EqualTolerance = true
  ExtensionAngle = 0
  FormatSpec = %.2w
  FormatSpecOverTolerance = %+.2w
  FormatSpecUnderTolerance = %+.2w
  Inverted = false
  LineAngle = 0
  LockPosition = false
  MeasureType = 1
  OverTolerance = 0
  References2D = -> [View021]
  Rotation = 0
  ScaleType = 0
  TheoreticalExact = false
  Type = 1
  UnderTolerance = 0
  X = 0
  Y = 33.7721
FEATURE [TechDraw::DrawViewDimension] Dimension088
  AngleOverride = false
  Arbitrary = false
  ArbitraryTolerances = false
  BoxCorners = (2) [(-36.3,-36.3,0),(36.3,36.3,0)]
  EqualTolerance = true
  ExtensionAngle = 0
  FormatSpec = %.2w
  FormatSpecOverTolerance = %+.2w
  FormatSpecUnderTolerance = %+.2w
  Inverted = false
  LineAngle = 0
  LockPosition = false
  MeasureType = 1
  OverTolerance = 0
  References2D = -> [View021]
  Rotation = 0
  ScaleType = 0
  TheoreticalExact = false
  Type = 2
  UnderTolerance = 0
  X = 38.5853
  Y = 17.1099
FEATURE [TechDraw::DrawViewDimension] Dimension089
  AngleOverride = false
  Arbitrary = false
  ArbitraryTolerances = false
  BoxCorners = (2) [(-36.3,-36.3,0),(36.3,36.3,0)]
  EqualTolerance = true
  ExtensionAngle = 0
  FormatSpec = %.2w
  FormatSpecOverTolerance = %+.2w
  FormatSpecUnderTolerance = %+.2w
  Inverted = false
  LineAngle = 0
  LockPosition = false
  MeasureType = 1
  OverTolerance = 0
  References2D = -> [View021]
  Rotation = 0
  ScaleType = 0
  TheoreticalExact = false
  Type = 2
  UnderTolerance = 0
  X = -49.5226
  Y = 16.5151
FEATURE [TechDraw::DrawProjGroupItem] View022  label="View023"
  CoarseView = false
  Direction = (0,-1,2)
  Focus = 100
  HardHidden = false
  IsoCount = 0
  IsoHidden = false
  IsoVisible = false
  LockPosition = false
  Perspective = false
  Rotation = 0
  RotationVector = (1,0,0)
  Scale = 0.5
  ScaleType = 2
  ScrubCount = 1
  SeamHidden = false
  SeamVisible = false
  SmoothHidden = false
  SmoothVisible = true
  Source = -> [Compound001]
  Type = 0
  X = 242.828
  XDirection = (1,0,0)
  Y = 45.965
FEATURE [TechDraw::DrawProjGroupItem] View023  label="View024"
  CoarseView = false
  Direction = (0,-1,0)
  Focus = 100
  HardHidden = false
  IsoCount = 0
  IsoHidden = false
  IsoVisible = false
  LockPosition = false
  Perspective = false
  Rotation = 0
  RotationVector = (1,0,0)
  ScaleType = 0
  ScrubCount = 1
  SeamHidden = false
  SeamVisible = false
  SmoothHidden = false
  SmoothVisible = true
  Source = -> [Compound]
  Type = 0
  X = 148.135
  XDirection = (1,0,0)
  Y = 114.131
FEATURE [TechDraw::DrawViewDimension] Dimension090
  AngleOverride = false
  Arbitrary = false
  ArbitraryTolerances = false
  BoxCorners = (2) [(-122.42,-41.015,-1e-07),(122.42,41.015,1e-07)]
  EqualTolerance = true
  ExtensionAngle = 0
  FormatSpec = %.2w
  FormatSpecOverTolerance = %+.2w
  FormatSpecUnderTolerance = %+.2w
  Inverted = false
  LineAngle = 0
  LockPosition = false
  MeasureType = 1
  OverTolerance = 0
  References2D = -> [View023]
  Rotation = 0
  ScaleType = 0
  TheoreticalExact = false
  Type = 1
  UnderTolerance = 0
  X = 0
  Y = -62.6456
FEATURE [TechDraw::DrawViewDimension] Dimension092
  AngleOverride = false
  Arbitrary = false
  ArbitraryTolerances = false
  BoxCorners = (2) [(-122.42,-41.015,-1e-07),(122.42,41.015,1e-07)]
  EqualTolerance = true
  ExtensionAngle = 0
  FormatSpec = %.2w
  FormatSpecOverTolerance = %+.2w
  FormatSpecUnderTolerance = %+.2w
  Inverted = false
  LineAngle = 0
  LockPosition = false
  MeasureType = 1
  OverTolerance = 0
  References2D = -> [View023]
  Rotation = 0
  ScaleType = 0
  TheoreticalExact = false
  Type = 2
  UnderTolerance = 0
  X = -135.254
  Y = -26.9
FEATURE [TechDraw::DrawViewDimension] Dimension094
  AngleOverride = false
  Arbitrary = false
  ArbitraryTolerances = false
  BoxCorners = (2) [(-122.42,-41.015,-1e-07),(122.42,41.015,1e-07)]
  EqualTolerance = true
  ExtensionAngle = 0
  FormatSpec = %.2w
  FormatSpecOverTolerance = %+.2w
  FormatSpecUnderTolerance = %+.2w
  Inverted = false
  LineAngle = 0
  LockPosition = false
  MeasureType = 1
  OverTolerance = 0
  References2D = -> [View023]
  Rotation = 0
  ScaleType = 0
  TheoreticalExact = false
  Type = 2
  UnderTolerance = 0
  X = -79.503
  Y = 18.7649
FEATURE [TechDraw::DrawViewDimension] Dimension095
  AngleOverride = false
  Arbitrary = false
  ArbitraryTolerances = false
  BoxCorners = (2) [(-122.42,-41.015,-1e-07),(122.42,41.015,1e-07)]
  EqualTolerance = true
  ExtensionAngle = 0
  FormatSpec = %.2w
  FormatSpecOverTolerance = %+.2w
  FormatSpecUnderTolerance = %+.2w
  Inverted = false
  LineAngle = 0
  LockPosition = false
  MeasureType = 1
  OverTolerance = 0
  References2D = -> [View023]
  Rotation = 0
  ScaleType = 0
  TheoreticalExact = false
  Type = 2
  UnderTolerance = 0
  X = 60.642
  Y = 54.1085
FEATURE [TechDraw::DrawViewAnnotation] Annotation
  Font = osifont
  LineSpace = 100
  LockPosition = false
  MaxWidth = -1
  Rotation = 0
  ScaleType = 0
  Text = groving the cyllinder
  TextSize = 5
  TextStyle = 0
  X = 121.901
  Y = 190.381
FEATURE [TechDraw::DrawSVGTemplate] Template
  Height = 210
  Orientation = 1
  Template = /app/share/Mod/TechDraw/Templates/Default_Template_A4_Landscape.svg
  Width = 297
FEATURE [TechDraw::DrawViewAnnotation] Annotation001
  Font = osifont
  LineSpace = 100
  LockPosition = false
  MaxWidth = -1
  Rotation = 0
  ScaleType = 0
  Text = PLATES
  TextSize = 5
  TextStyle = 0
  X = 255.694
  Y = 150.94
FEATURE [TechDraw::DrawSVGTemplate] Template005
  Height = 210
  Orientation = 1
  Template = /app/share/Mod/TechDraw/Templates/Default_Template_A4_Landscape.svg
  Width = 297
FEATURE [TechDraw::DrawProjGroupItem] View029  label="View030"
  CoarseView = false
  Direction = (2e-16,1,0)
  Focus = 100
  HardHidden = false
  IsoCount = 0
  IsoHidden = false
  IsoVisible = false
  LockPosition = false
  Perspective = false
  Rotation = 0
  RotationVector = (1,0,0)
  Scale = 0.5
  ScaleType = 2
  ScrubCount = 1
  SeamHidden = false
  SeamVisible = false
  SmoothHidden = false
  SmoothVisible = true
  Source = -> [Compound]
  Type = 0
  X = 69.0915
  XDirection = (-1,2e-16,0)
  Y = 152.996
FEATURE [TechDraw::DrawProjGroupItem] View030  label="View031"
  CoarseView = false
  Direction = (2e-16,2,1)
  Focus = 100
  HardHidden = false
  IsoCount = 0
  IsoHidden = false
  IsoVisible = false
  LockPosition = false
  Perspective = false
  Rotation = 0
  RotationVector = (1,0,0)
  Scale = 0.5
  ScaleType = 2
  ScrubCount = 1
  SeamHidden = false
  SeamVisible = false
  SmoothHidden = false
  SmoothVisible = true
  Source = -> [Compound]
  Type = 0
  X = 76.5648
  XDirection = (-1,2e-16,0)
  Y = 52.4295
FEATURE [TechDraw::DrawProjGroupItem] View031  label="View032"
  CoarseView = false
  Direction = (0,0,1)
  Focus = 100
  HardHidden = false
  IsoCount = 0
  IsoHidden = false
  IsoVisible = false
  LockPosition = false
  Perspective = false
  Rotation = 0
  RotationVector = (1,0,0)
  Scale = 0.666667
  ScaleType = 2
  ScrubCount = 1
  SeamHidden = false
  SeamVisible = false
  SmoothHidden = false
  SmoothVisible = true
  Source = -> [Compound]
  Type = 0
  X = 213.371
  XDirection = (1,0,0)
  Y = 109.217
FEATURE [TechDraw::DrawViewDimension] Dimension113
  AngleOverride = false
  Arbitrary = false
  ArbitraryTolerances = false
  BoxCorners = (2) [(-61.21,-61.21,0),(61.21,61.21,0)]
  EqualTolerance = true
  ExtensionAngle = 0
  FormatSpec = %.2w
  FormatSpecOverTolerance = %+.2w
  FormatSpecUnderTolerance = %+.2w
  Inverted = false
  LineAngle = 0
  LockPosition = false
  MeasureType = 1
  OverTolerance = 0
  References2D = -> [View031]
  Rotation = 0
  ScaleType = 0
  TheoreticalExact = false
  Type = 1
  UnderTolerance = 0
  X = 0
  Y = 36.3485
FEATURE [TechDraw::DrawViewDimension] Dimension114
  AngleOverride = false
  Arbitrary = false
  ArbitraryTolerances = false
  BoxCorners = (2) [(-61.21,-61.21,0),(61.21,61.21,0)]
  EqualTolerance = true
  ExtensionAngle = 0
  FormatSpec = %.2w
  FormatSpecOverTolerance = %+.2w
  FormatSpecUnderTolerance = %+.2w
  Inverted = false
  LineAngle = 0
  LockPosition = false
  MeasureType = 1
  OverTolerance = 0
  References2D = -> [View031]
  Rotation = 0
  ScaleType = 0
  TheoreticalExact = false
  Type = 2
  UnderTolerance = 0
  X = 25.4038
  Y = 32.5692
FEATURE [TechDraw::DrawViewDimension] Dimension115
  AngleOverride = false
  Arbitrary = false
  ArbitraryTolerances = false
  BoxCorners = (2) [(-61.21,-61.21,0),(61.21,61.21,0)]
  EqualTolerance = true
  ExtensionAngle = 0
  FormatSpec = %.2w
  FormatSpecOverTolerance = %+.2w
  FormatSpecUnderTolerance = %+.2w
  Inverted = false
  LineAngle = 0
  LockPosition = false
  MeasureType = 1
  OverTolerance = 0
  References2D = -> [View031]
  Rotation = 0
  ScaleType = 0
  TheoreticalExact = false
  Type = 2
  UnderTolerance = 0
  X = -35.9925
  Y = 29.267
FEATURE [TechDraw::DrawViewDimension] Dimension116
  AngleOverride = false
  Arbitrary = false
  ArbitraryTolerances = false
  BoxCorners = (2) [(-61.21,-61.21,0),(61.21,61.21,0)]
  EqualTolerance = true
  ExtensionAngle = 0
  FormatSpec = ⌀%.2w
  FormatSpecOverTolerance = %+.2w
  FormatSpecUnderTolerance = %+.2w
  Inverted = false
  LineAngle = 0
  LockPosition = false
  MeasureType = 1
  OverTolerance = 0
  References2D = -> [View031]
  Rotation = 0
  ScaleType = 0
  TheoreticalExact = false
  Type = 5
  UnderTolerance = 0
  X = -47.5972
  Y = -9.28739
FEATURE [TechDraw::DrawViewDimension] Dimension117
  AngleOverride = false
  Arbitrary = false
  ArbitraryTolerances = false
  BoxCorners = (2) [(-61.21,-61.21,0),(61.21,61.21,0)]
  EqualTolerance = true
  ExtensionAngle = 0
  FormatSpec = ⌀%.2w
  FormatSpecOverTolerance = %+.2w
  FormatSpecUnderTolerance = %+.2w
  Inverted = false
  LineAngle = 0
  LockPosition = false
  MeasureType = 1
  OverTolerance = 0
  References2D = -> [View031]
  Rotation = 0
  ScaleType = 0
  TheoreticalExact = false
  Type = 5
  UnderTolerance = 0
  X = -46.6029
  Y = 3.63682
FEATURE [TechDraw::DrawViewAnnotation] Annotation003
  Font = osifont
  LineSpace = 100
  LockPosition = false
  MaxWidth = -1
  Rotation = 0
  ScaleType = 0
  Text = keying the cylinder
  TextSize = 5
  TextStyle = 0
  X = 98.1404
  Y = 199.949
FEATURE [TechDraw::DrawSVGTemplate] Template006
  Height = 210
  Orientation = 1
  Template = /app/share/Mod/TechDraw/Templates/Default_Template_A4_Landscape.svg
  Width = 297
FEATURE [TechDraw::DrawProjGroupItem] View032  label="View033"
  CoarseView = false
  Direction = (0,0,-1)
  Focus = 100
  HardHidden = false
  IsoCount = 0
  IsoHidden = false
  IsoVisible = false
  LockPosition = false
  Perspective = false
  Rotation = 0
  RotationVector = (1,0,0)
  Scale = 0.4
  ScaleType = 2
  ScrubCount = 1
  SeamHidden = false
  SeamVisible = false
  SmoothHidden = false
  SmoothVisible = true
  Source = -> [Compound]
  Type = 0
  X = 121.483
  XDirection = (1,0,0)
  Y = 132.685
FEATURE [TechDraw::DrawProjGroupItem] View
  CoarseView = false
  Direction = (0,-1,0)
  Focus = 100
  HardHidden = false
  IsoCount = 0
  IsoHidden = false
  IsoVisible = false
  LockPosition = false
  Perspective = false
  Rotation = 0
  RotationVector = (1,0,0)
  ScaleType = 0
  ScrubCount = 1
  SeamHidden = false
  SeamVisible = false
  SmoothHidden = false
  SmoothVisible = true
  Source = -> [Compound]
  Type = 0
  X = 150.44
  XDirection = (1,0,0)
  Y = 156.907
FEATURE [TechDraw::DrawViewSection] SectionView  label="Section  - "
  BaseView = -> View032
  CoarseView = false
  CutSurfaceDisplay = 2
  Direction = (1,0,0)
  FileGeomPattern = /app/share/Mod/TechDraw/PAT/FCPAT.pat
  FileHatchPattern = /app/share/Mod/TechDraw/Patterns/simple.svg
  Focus = 100
  FuseBeforeCut = false
  HardHidden = false
  HatchOffset = (0,0,0)
  HatchRotation = 0
  HatchScale = 1
  IsoCount = 0
  IsoHidden = false
  IsoVisible = false
  LockPosition = false
  NameGeomPattern = Diamond
  Perspective = false
  Rotation = -90
  Scale = 0.5
  ScaleType = 2
  ScrubCount = 1
  SeamHidden = false
  SeamVisible = false
  SectionDirection = 4
  SectionLineStretch = 1
  SectionNormal = (1,0,0)
  SectionOrigin = (0,-5,41.02)
  SmoothHidden = false
  SmoothVisible = true
  Source = -> [Compound]
  TrimAfterCut = false
  UsePreviousCut = false
  X = 218.373
  XDirection = (1e-16,1,0)
  Y = 73.6685
FEATURE [TechDraw::DrawViewDimension] Dimension120
  AngleOverride = false
  Arbitrary = false
  ArbitraryTolerances = false
  BoxCorners = (2) [(-61.275,-61.275,0),(61.275,61.275,0)]
  EqualTolerance = true
  ExtensionAngle = 0
  FormatSpec = ⌀%.2w
  FormatSpecOverTolerance = %+.2w
  FormatSpecUnderTolerance = %+.2w
  Inverted = false
  LineAngle = 0
  LockPosition = false
  MeasureType = 1
  OverTolerance = 0
  References2D = -> [View032]
  Rotation = 0
  ScaleType = 0
  TheoreticalExact = false
  Type = 5
  UnderTolerance = 0
  X = -26.946
  Y = -24.1513
FEATURE [TechDraw::DrawViewDimension] Dimension121
  AngleOverride = false
  Arbitrary = false
  ArbitraryTolerances = false
  BoxCorners = (2) [(-122.55,-41.015,-1e-07),(122.55,41.015,1e-07)]
  EqualTolerance = true
  ExtensionAngle = 0
  FormatSpec = %.2w
  FormatSpecOverTolerance = %+.2w
  FormatSpecUnderTolerance = %+.2w
  Inverted = false
  LineAngle = 0
  LockPosition = false
  MeasureType = 1
  OverTolerance = 0
  References2D = -> [View]
  Rotation = 0
  ScaleType = 0
  TheoreticalExact = false
  Type = 2
  UnderTolerance = 0
  X = -133.97
  Y = -27.5
FEATURE [TechDraw::DrawViewDimension] Dimension122
  AngleOverride = false
  Arbitrary = false
  ArbitraryTolerances = false
  BoxCorners = (2) [(-122.55,-41.015,-1e-07),(122.55,41.015,1e-07)]
  EqualTolerance = true
  ExtensionAngle = 0
  FormatSpec = %.2w
  FormatSpecOverTolerance = %+.2w
  FormatSpecUnderTolerance = %+.2w
  Inverted = false
  LineAngle = 0
  LockPosition = false
  MeasureType = 1
  OverTolerance = 0
  References2D = -> [View]
  Rotation = 0
  ScaleType = 0
  TheoreticalExact = false
  Type = 2
  UnderTolerance = 0
  X = -133.97
  Y = 14.5
FEATURE [TechDraw::DrawViewDimension] Dimension125
  AngleOverride = false
  Arbitrary = false
  ArbitraryTolerances = false
  BoxCorners = (2) [(-122.55,-42,-1e-07),(122.55,42,1e-07)]
  EqualTolerance = true
  ExtensionAngle = 0
  FormatSpec = %.2w
  FormatSpecOverTolerance = %+.2w
  FormatSpecUnderTolerance = %+.2w
  Inverted = false
  LineAngle = 0
  LockPosition = false
  MeasureType = 1
  OverTolerance = 0
  References2D = -> [View]
  Rotation = 0
  ScaleType = 0
  TheoreticalExact = false
  Type = 1
  UnderTolerance = 0
  X = 0
  Y = -25.1885
FEATURE [TechDraw::DrawViewDimension] Dimension126
  AngleOverride = false
  Arbitrary = false
  ArbitraryTolerances = false
  BoxCorners = (2) [(-122.55,-42,-1e-07),(122.55,42,1e-07)]
  EqualTolerance = true
  ExtensionAngle = 0
  FormatSpec = %.2w
  FormatSpecOverTolerance = %+.2w
  FormatSpecUnderTolerance = %+.2w
  Inverted = false
  LineAngle = 0
  LockPosition = false
  MeasureType = 1
  OverTolerance = 0
  References2D = -> [View]
  Rotation = 0
  ScaleType = 0
  TheoreticalExact = false
  Type = 1
  UnderTolerance = 0
  X = 0
  Y = 18.7522
FEATURE [TechDraw::DrawViewDimension] Dimension127
  AngleOverride = false
  Arbitrary = false
  ArbitraryTolerances = false
  BoxCorners = (2) [(-122.55,-42,-1e-07),(122.55,42,1e-07)]
  EqualTolerance = true
  ExtensionAngle = 0
  FormatSpec = %.2w
  FormatSpecOverTolerance = %+.2w
  FormatSpecUnderTolerance = %+.2w
  Inverted = false
  LineAngle = 0
  LockPosition = false
  MeasureType = 1
  OverTolerance = 0
  References2D = -> [View]
  Rotation = 0
  ScaleType = 0
  TheoreticalExact = false
  Type = 2
  UnderTolerance = 0
  X = -145.406
  Y = -4.55405
FEATURE [TechDraw::DrawViewDimension] Dimension132
  AngleOverride = false
  Arbitrary = false
  ArbitraryTolerances = false
  BoxCorners = (2) [(-122.5,-42,-1e-07),(122.5,42,1e-07)]
  EqualTolerance = true
  ExtensionAngle = 0
  FormatSpec = %.2w
  FormatSpecOverTolerance = %+.2w
  FormatSpecUnderTolerance = %+.2w
  Inverted = false
  LineAngle = 0
  LockPosition = false
  MeasureType = 1
  OverTolerance = 0
  References2D = -> [View]
  Rotation = 0
  ScaleType = 0
  TheoreticalExact = false
  Type = 2
  UnderTolerance = 0
  X = 127.862
  Y = -28.0474
FEATURE [TechDraw::DrawViewDimension] Dimension133
  AngleOverride = false
  Arbitrary = false
  ArbitraryTolerances = false
  BoxCorners = (2) [(-21,-61.25,-1e-07),(21,61.25,1e-07)]
  EqualTolerance = true
  ExtensionAngle = 0
  FormatSpec = %.2w
  FormatSpecOverTolerance = %+.2w
  FormatSpecUnderTolerance = %+.2w
  Inverted = false
  LineAngle = 0
  LockPosition = false
  MeasureType = 1
  OverTolerance = 0
  References2D = -> [SectionView]
  Rotation = 0
  ScaleType = 0
  TheoreticalExact = false
  Type = 1
  UnderTolerance = 0
  X = 7.17079
  Y = -20.5091
FEATURE [TechDraw::DrawViewDimension] Dimension135
  AngleOverride = false
  Arbitrary = false
  ArbitraryTolerances = false
  BoxCorners = (2) [(-21,-61.25,-1e-07),(21,61.25,1e-07)]
  EqualTolerance = true
  ExtensionAngle = 0
  FormatSpec = %.2w
  FormatSpecOverTolerance = %+.2w
  FormatSpecUnderTolerance = %+.2w
  Inverted = false
  LineAngle = 0
  LockPosition = false
  MeasureType = 1
  OverTolerance = 0
  References2D = -> [SectionView]
  Rotation = 0
  ScaleType = 0
  TheoreticalExact = false
  Type = 2
  UnderTolerance = 0
  X = 44.1361
  Y = 0
FEATURE [TechDraw::DrawViewDimension] Dimension136
  AngleOverride = false
  Arbitrary = false
  ArbitraryTolerances = false
  BoxCorners = (2) [(-21,-61.25,-1e-07),(21,61.25,1e-07)]
  EqualTolerance = true
  ExtensionAngle = 0
  FormatSpec = %.2w
  FormatSpecOverTolerance = %+.2w
  FormatSpecUnderTolerance = %+.2w
  Inverted = false
  LineAngle = 0
  LockPosition = false
  MeasureType = 1
  OverTolerance = 0
  References2D = -> [SectionView]
  Rotation = 0
  ScaleType = 0
  TheoreticalExact = false
  Type = 2
  UnderTolerance = 0
  X = 27.2502
  Y = 12.2253
FEATURE [TechDraw::DrawViewDimension] Dimension
  AngleOverride = false
  Arbitrary = false
  ArbitraryTolerances = false
  BoxCorners = (2) [(-61.25,-61.25,0),(61.25,61.25,0)]
  EqualTolerance = true
  ExtensionAngle = 0
  FormatSpec = ⌀%.2w
  FormatSpecOverTolerance = %+.2w
  FormatSpecUnderTolerance = %+.2w
  Inverted = false
  LineAngle = 0
  LockPosition = false
  MeasureType = 1
  OverTolerance = 0
  References2D = -> [View032]
  Rotation = 0
  ScaleType = 0
  TheoreticalExact = false
  Type = 5
  UnderTolerance = 0
  X = -39.3088
  Y = 4.36988
FEATURE [TechDraw::DrawViewDimension] Dimension137
  AngleOverride = false
  Arbitrary = false
  ArbitraryTolerances = false
  BoxCorners = (2) [(-61.25,-61.25,0),(61.25,61.25,0)]
  EqualTolerance = true
  ExtensionAngle = 0
  FormatSpec = ⌀%.2w
  FormatSpecOverTolerance = %+.2w
  FormatSpecUnderTolerance = %+.2w
  Inverted = false
  LineAngle = 0
  LockPosition = false
  MeasureType = 1
  OverTolerance = 0
  References2D = -> [View032]
  Rotation = 0
  ScaleType = 0
  TheoreticalExact = false
  Type = 5
  UnderTolerance = 0
  X = -10.4244
  Y = 12.393
FEATURE [TechDraw::DrawViewDimension] Dimension138
  AngleOverride = false
  Arbitrary = false
  ArbitraryTolerances = false
  BoxCorners = (2) [(-21,-61.25,-1e-07),(21,61.25,1e-07)]
  EqualTolerance = true
  ExtensionAngle = 0
  FormatSpec = %.2w
  FormatSpecOverTolerance = %+.2w
  FormatSpecUnderTolerance = %+.2w
  Inverted = false
  LineAngle = 0
  LockPosition = false
  MeasureType = 1
  OverTolerance = 0
  References2D = -> [SectionView]
  Rotation = 0
  ScaleType = 0
  TheoreticalExact = false
  Type = 2
  UnderTolerance = 0
  X = -48.7843
  Y = 4.08697
FEATURE [TechDraw::DrawViewDimension] Dimension139
  AngleOverride = false
  Arbitrary = false
  ArbitraryTolerances = false
  BoxCorners = (2) [(-21,-61.25,-1e-07),(21,61.25,1e-07)]
  EqualTolerance = true
  ExtensionAngle = 0
  FormatSpec = %.2w
  FormatSpecOverTolerance = %+.2w
  FormatSpecUnderTolerance = %+.2w
  Inverted = false
  LineAngle = 0
  LockPosition = false
  MeasureType = 1
  OverTolerance = 0
  References2D = -> [SectionView]
  Rotation = 0
  ScaleType = 0
  TheoreticalExact = false
  Type = 1
  UnderTolerance = 0
  X = -33.1411
  Y = 16.9125
FEATURE [TechDraw::DrawViewSection] SectionView001  label="Section001  - "
  BaseView = -> View
  CoarseView = false
  CutSurfaceDisplay = 2
  Direction = (1e-16,0,1)
  FileGeomPattern = /app/share/Mod/TechDraw/PAT/FCPAT.pat
  FileHatchPattern = /app/share/Mod/TechDraw/Patterns/simple.svg
  Focus = 100
  FuseBeforeCut = false
  HardHidden = false
  HatchOffset = (0,0,0)
  HatchRotation = 0
  HatchScale = 1
  IsoCount = 0
  IsoHidden = false
  IsoVisible = false
  LockPosition = false
  NameGeomPattern = Diamond
  Perspective = false
  Rotation = 0
  Scale = 0.45
  ScaleType = 2
  ScrubCount = 1
  SeamHidden = false
  SeamVisible = false
  SectionDirection = 4
  SectionLineStretch = 1
  SectionNormal = (1e-16,0,1)
  SectionOrigin = (0,0,42)
  SmoothHidden = false
  SmoothVisible = true
  Source = -> [Compound]
  TrimAfterCut = false
  UsePreviousCut = false
  X = 235.082
  XDirection = (1,0,-1e-16)
  Y = 57.1775
FEATURE [TechDraw::DrawViewDimension] Dimension140
  AngleOverride = false
  Arbitrary = false
  ArbitraryTolerances = false
  BoxCorners = (2) [(-55.125,-55.125,0),(55.125,55.125,0)]
  EqualTolerance = true
  ExtensionAngle = 0
  FormatSpec = ⌀%.2w
  FormatSpecOverTolerance = %+.2w
  FormatSpecUnderTolerance = %+.2w
  Inverted = false
  LineAngle = 0
  LockPosition = false
  MeasureType = 1
  OverTolerance = 0
  References2D = -> [SectionView001]
  Rotation = 0
  ScaleType = 0
  TheoreticalExact = false
  Type = 5
  UnderTolerance = 0
  X = -28.6137
  Y = -22.0728
FEATURE [TechDraw::DrawViewDimension] Dimension141
  AngleOverride = false
  Arbitrary = false
  ArbitraryTolerances = false
  BoxCorners = (2) [(-55.125,-55.125,0),(55.125,55.125,0)]
  EqualTolerance = true
  ExtensionAngle = 0
  FormatSpec = ⌀%.2w
  FormatSpecOverTolerance = %+.2w
  FormatSpecUnderTolerance = %+.2w
  Inverted = false
  LineAngle = 0
  LockPosition = false
  MeasureType = 1
  OverTolerance = 0
  References2D = -> [SectionView001]
  Rotation = 0
  ScaleType = 0
  TheoreticalExact = false
  Type = 5
  UnderTolerance = 0
  X = -30.7891
  Y = 8.25939
FEATURE [TechDraw::DrawViewDimension] Dimension142
  AngleOverride = false
  Arbitrary = false
  ArbitraryTolerances = false
  BoxCorners = (2) [(-55.125,-55.125,0),(55.125,55.125,0)]
  EqualTolerance = true
  ExtensionAngle = 0
  FormatSpec = ⌀%.2w
  FormatSpecOverTolerance = %+.2w
  FormatSpecUnderTolerance = %+.2w
  Inverted = false
  LineAngle = 0
  LockPosition = false
  MeasureType = 1
  OverTolerance = 0
  References2D = -> [SectionView001]
  Rotation = 0
  ScaleType = 0
  TheoreticalExact = false
  Type = 5
  UnderTolerance = 0
  X = -24.3333
  Y = 20.7728
FEATURE [TechDraw::DrawViewImage] ActiveView
  Height = 102.4
  ImageFile = <userpath>/.var/app/org.freecad.FreeCAD/cache/FreeCAD/Cache/FreeCAD_Doc_e07cf831-7cb1-4124-b06d-c17eae93a098_c6ff8a_767782/PageActiveViewZJGMVF.png
  LockPosition = false
  Rotation = 0
  ScaleType = 2
  Width = 128
  X = 63.5722
  Y = 64.1875
FEATURE [TechDraw::DrawViewImage] ActiveView001
  Height = 102.4
  ImageFile = <userpath>/.var/app/org.freecad.FreeCAD/cache/FreeCAD/Cache/FreeCAD_Doc_e07cf831-7cb1-4124-b06d-c17eae93a098_c6ff8a_767782/PageActiveView001sZ93KP.png
  LockPosition = false
  Rotation = 0
  ScaleType = 2
  Width = 128
  X = 134.57
  Y = 64.1875
FEATURE [TechDraw::DrawViewDimension] Dimension143
  AngleOverride = false
  Arbitrary = false
  ArbitraryTolerances = false
  BoxCorners = (2) [(-122.5,-42,-1e-07),(122.5,42,1e-07)]
  EqualTolerance = true
  ExtensionAngle = 0
  FormatSpec = %.2w
  FormatSpecOverTolerance = %+.2w
  FormatSpecUnderTolerance = %+.2w
  Inverted = false
  LineAngle = 0
  LockPosition = false
  MeasureType = 1
  OverTolerance = 0
  References2D = -> [View023]
  Rotation = 0
  ScaleType = 0
  TheoreticalExact = false
  Type = 1
  UnderTolerance = 0
  X = 0
  Y = 9.30427
FEATURE [TechDraw::DrawViewDimension] Dimension146
  AngleOverride = false
  Arbitrary = false
  ArbitraryTolerances = false
  BoxCorners = (2) [(-122.5,-42,-1e-07),(122.5,42,1e-07)]
  EqualTolerance = true
  ExtensionAngle = 0
  FormatSpec = %.2w
  FormatSpecOverTolerance = %+.2w
  FormatSpecUnderTolerance = %+.2w
  Inverted = false
  LineAngle = 0
  LockPosition = false
  MeasureType = 1
  OverTolerance = 0
  References2D = -> [View023]
  Rotation = 0
  ScaleType = 0
  TheoreticalExact = false
  Type = 1
  UnderTolerance = 0
  X = 29.4092
  Y = 33.4278
FEATURE [TechDraw::DrawViewDimension] Dimension147
  AngleOverride = false
  Arbitrary = false
  ArbitraryTolerances = false
  BoxCorners = (2) [(-122.5,-42,-1e-07),(122.5,42,1e-07)]
  EqualTolerance = true
  ExtensionAngle = 0
  FormatSpec = %.2w
  FormatSpecOverTolerance = %+.2w
  FormatSpecUnderTolerance = %+.2w
  Inverted = false
  LineAngle = 0
  LockPosition = false
  MeasureType = 1
  OverTolerance = 0
  References2D = -> [View023]
  Rotation = 0
  ScaleType = 0
  TheoreticalExact = false
  Type = 1
  UnderTolerance = 0
  X = -28.0463
  Y = 56.7968
FEATURE [TechDraw::DrawPage] Page004  label="grove"
  KeepUpdated = true
  NextBalloonIndex = 1
  ProjectionType = 0
  Template = -> Template004
  Views = -> [View023,Dimension090,Dimension092,Dimension094,Dimension095,Annotation,Dimension143,Dimension146,Dimension147]
FEATURE [TechDraw::DrawViewAnnotation] Annotation004
  Font = osifont
  LineSpace = 100
  LockPosition = false
  MaxWidth = -1
  Rotation = 0
  ScaleType = 0
  Text = Shaping cylinder | carving extending drum
  TextSize = 5
  TextStyle = 0
  X = 252.725
  Y = 192.718
FEATURE [TechDraw::DrawViewDimension] Dimension148
  AngleOverride = false
  Arbitrary = false
  ArbitraryTolerances = false
  BoxCorners = (2) [(-55.125,-55.125,0),(55.125,55.125,0)]
  EqualTolerance = true
  ExtensionAngle = 0
  FormatSpec = ⌀%.2w
  FormatSpecOverTolerance = %+.2w
  FormatSpecUnderTolerance = %+.2w
  Inverted = false
  LineAngle = 0
  LockPosition = false
  MeasureType = 1
  OverTolerance = 0
  References2D = -> [SectionView001]
  Rotation = 0
  ScaleType = 0
  TheoreticalExact = false
  Type = 5
  UnderTolerance = 0
  X = -11.8775
  Y = 29.2866
FEATURE [TechDraw::DrawPage] Page  label="cylinderShaping"
  KeepUpdated = true
  NextBalloonIndex = 1
  ProjectionType = 0
  Template = -> Template
  Views = -> [View,Dimension121,Dimension122,Dimension125,Dimension126,Dimension127,Dimension132,SectionView001,Dimension140,Dimension141,Dimension142,ActiveView,ActiveView001,Annotation004,Dimension148]
FEATURE [TechDraw::DrawViewImage] ActiveView002
  Height = 102.4
  ImageFile = <userpath>/.var/app/org.freecad.FreeCAD/cache/FreeCAD/Cache/FreeCAD_Doc_e07cf831-7cb1-4124-b06d-c17eae93a098_c6ff8a_767782/Page006ActiveView002xgBU0Q.png
  LockPosition = false
  Rotation = 0
  ScaleType = 2
  Width = 128
  X = 268.271
  Y = 157.449
FEATURE [TechDraw::DrawViewImage] ActiveView003
  Height = 102.4
  ImageFile = <userpath>/.var/app/org.freecad.FreeCAD/cache/FreeCAD/Cache/FreeCAD_Doc_e07cf831-7cb1-4124-b06d-c17eae93a098_c6ff8a_767782/Page006ActiveView003nAKnZo.png
  LockPosition = false
  Rotation = 0
  ScaleType = 2
  Width = 128
  X = 67.0039
  Y = 151.279
FEATURE [TechDraw::DrawViewImage] ActiveView004
  Height = 102.4
  ImageFile = <userpath>/.var/app/org.freecad.FreeCAD/cache/FreeCAD/Cache/FreeCAD_Doc_e07cf831-7cb1-4124-b06d-c17eae93a098_c6ff8a_767782/Page006ActiveView0041Nj59a.png
  LockPosition = false
  Rotation = 0
  ScaleType = 2
  Width = 128
  X = 67.0039
  Y = 49.4282
FEATURE [TechDraw::DrawViewAnnotation] Annotation005
  Font = osifont
  LineSpace = 100
  LockPosition = false
  MaxWidth = -1
  Rotation = 0
  ScaleType = 0
  Text = cutting for fixing disk
  TextSize = 5
  TextStyle = 0
  X = 174.449
  Y = 186.091
FEATURE [TechDraw::DrawPage] Page006  label="diskFit_cutting"
  KeepUpdated = true
  NextBalloonIndex = 1
  ProjectionType = 0
  Template = -> Template006
  Views = -> [View032,SectionView,Dimension120,Dimension133,Dimension135,Dimension136,Dimension,Dimension137,Dimension138,Dimension139,ActiveView002,ActiveView003,ActiveView004,Annotation005]
FEATURE [TechDraw::DrawViewDimension] Dimension149
  AngleOverride = false
  Arbitrary = false
  ArbitraryTolerances = false
  BoxCorners = (2) [(-99.6,-24,-1e-07),(99.6,24,1e-07)]
  EqualTolerance = true
  ExtensionAngle = 0
  FormatSpec = %.2w
  FormatSpecOverTolerance = %+.2w
  FormatSpecUnderTolerance = %+.2w
  Inverted = false
  LineAngle = 0
  LockPosition = false
  MeasureType = 1
  OverTolerance = 0
  References2D = -> [View019]
  Rotation = 0
  ScaleType = 0
  TheoreticalExact = false
  Type = 1
  UnderTolerance = 0
  X = 0
  Y = 90.2732
FEATURE [TechDraw::DrawPage] Page003  label="plates"
  KeepUpdated = true
  NextBalloonIndex = 1
  ProjectionType = 0
  Template = -> Template003
  Views = -> [View019,Dimension079,Dimension080,Dimension081,Dimension082,Dimension083,Dimension084,Dimension085,View021,Dimension087,Dimension088,Dimension089,View022,Annotation001,Dimension149]
FEATURE [TechDraw::DrawViewDimension] Dimension150
  AngleOverride = false
  Arbitrary = false
  ArbitraryTolerances = false
  BoxCorners = (2) [(-61.25,-21,-1e-07),(61.25,21,1e-07)]
  EqualTolerance = true
  ExtensionAngle = 0
  FormatSpec = %.2w
  FormatSpecOverTolerance = %+.2w
  FormatSpecUnderTolerance = %+.2w
  Inverted = false
  LineAngle = 0
  LockPosition = false
  MeasureType = 1
  OverTolerance = 0
  References2D = -> [View029]
  Rotation = 0
  ScaleType = 0
  TheoreticalExact = false
  Type = 2
  UnderTolerance = 0
  X = -36.2514
  Y = 7.25
FEATURE [TechDraw::DrawPage] Page005  label="keying the cylinder"
  KeepUpdated = true
  NextBalloonIndex = 1
  ProjectionType = 0
  Template = -> Template005
  Views = -> [View029,View030,View031,Dimension113,Dimension114,Dimension115,Dimension116,Dimension117,Annotation003,Dimension150]
FEATURE [App::DocumentObjectGroup] Group001  label="drawings"
  Group = -> [Page,Page004,Page005,Page006,Page003]
